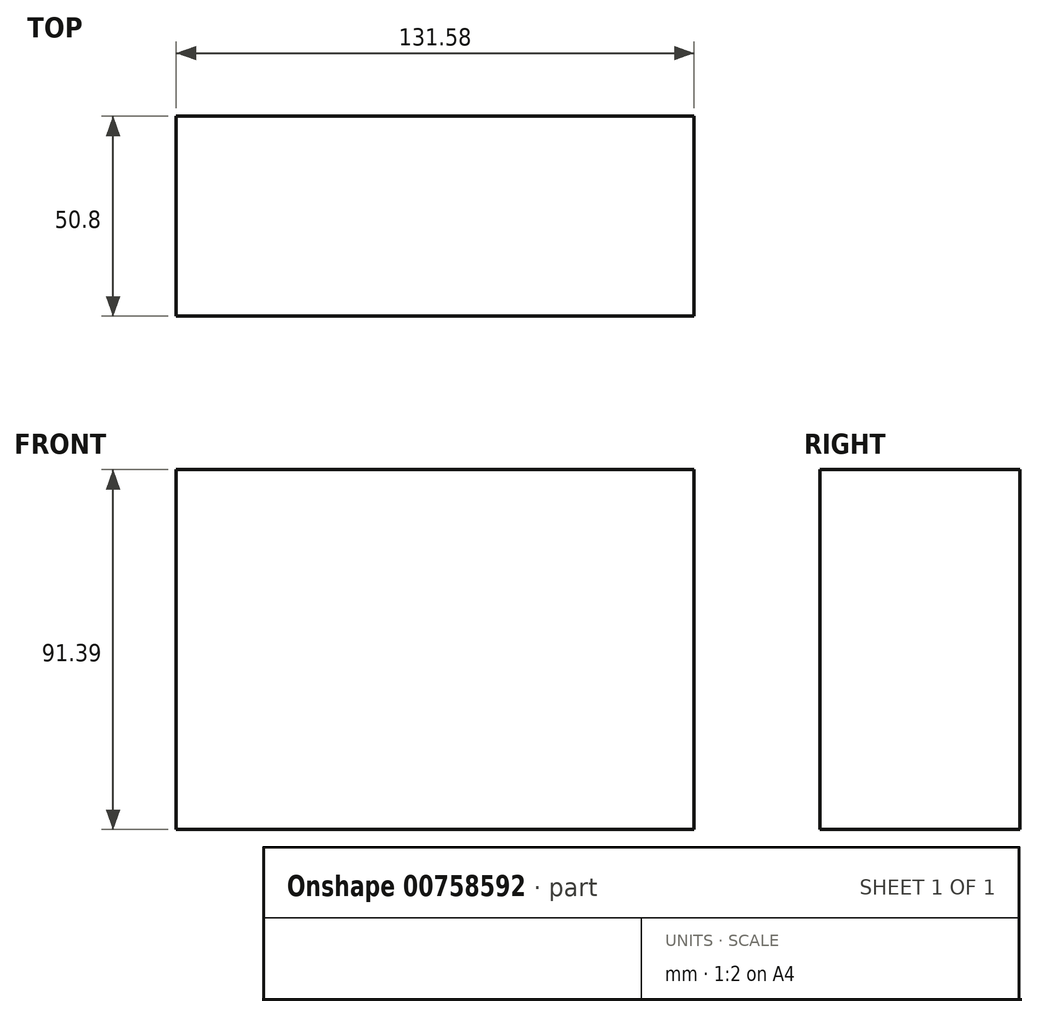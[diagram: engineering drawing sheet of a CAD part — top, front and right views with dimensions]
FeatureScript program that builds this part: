
annotation { "Feature Type Name" : "Feature", "Feature Type Description" : "" }
export const myFeature = defineFeature(function(context is Context, id is Id, definition is map)
    precondition{}
    {
        {
            var Q0;
            Q0=qCreatedBy(makeId("Front.planeOp"),FACE);
            var sketch = newSketch(context, id + "F0", { "sketchPlane" : qUnion([Q0])});
            skLineSegment(sketch, "E0.bottom", {"start": v(-55.08, 27.97) * mm, "end": v(76.5, 27.97) * mm});
            skLineSegment(sketch, "E0.top", {"start": v(-55.08, -63.42) * mm, "end": v(76.5, -63.42) * mm});
            skLineSegment(sketch, "E0.left", {"start": v(-55.08, 27.97) * mm, "end": v(-55.08, -63.42) * mm});
            skLineSegment(sketch, "E0.right", {"start": v(76.5, 27.97) * mm, "end": v(76.5, -63.42) * mm});
            skSolve(sketch);
        }
        {
            var Q0;
            Q0=makeQuery(id+"F0.imprint","IMPRINT",FACE,{"disambiguationData":[TD([[makeQuery(id+"F0.imprint","IMPRINT",EDGE,{"derivedFrom":sQuery(id+"F0.wireOp",EDGE,"E0.bottom")}),-1.0]])]});
            extrude(context, id + "F1", {"entities" : qUnion([Q0]), "depth" : 50.8 * mm, "offsetDistance" : 25.4 * mm});
        }
    });
